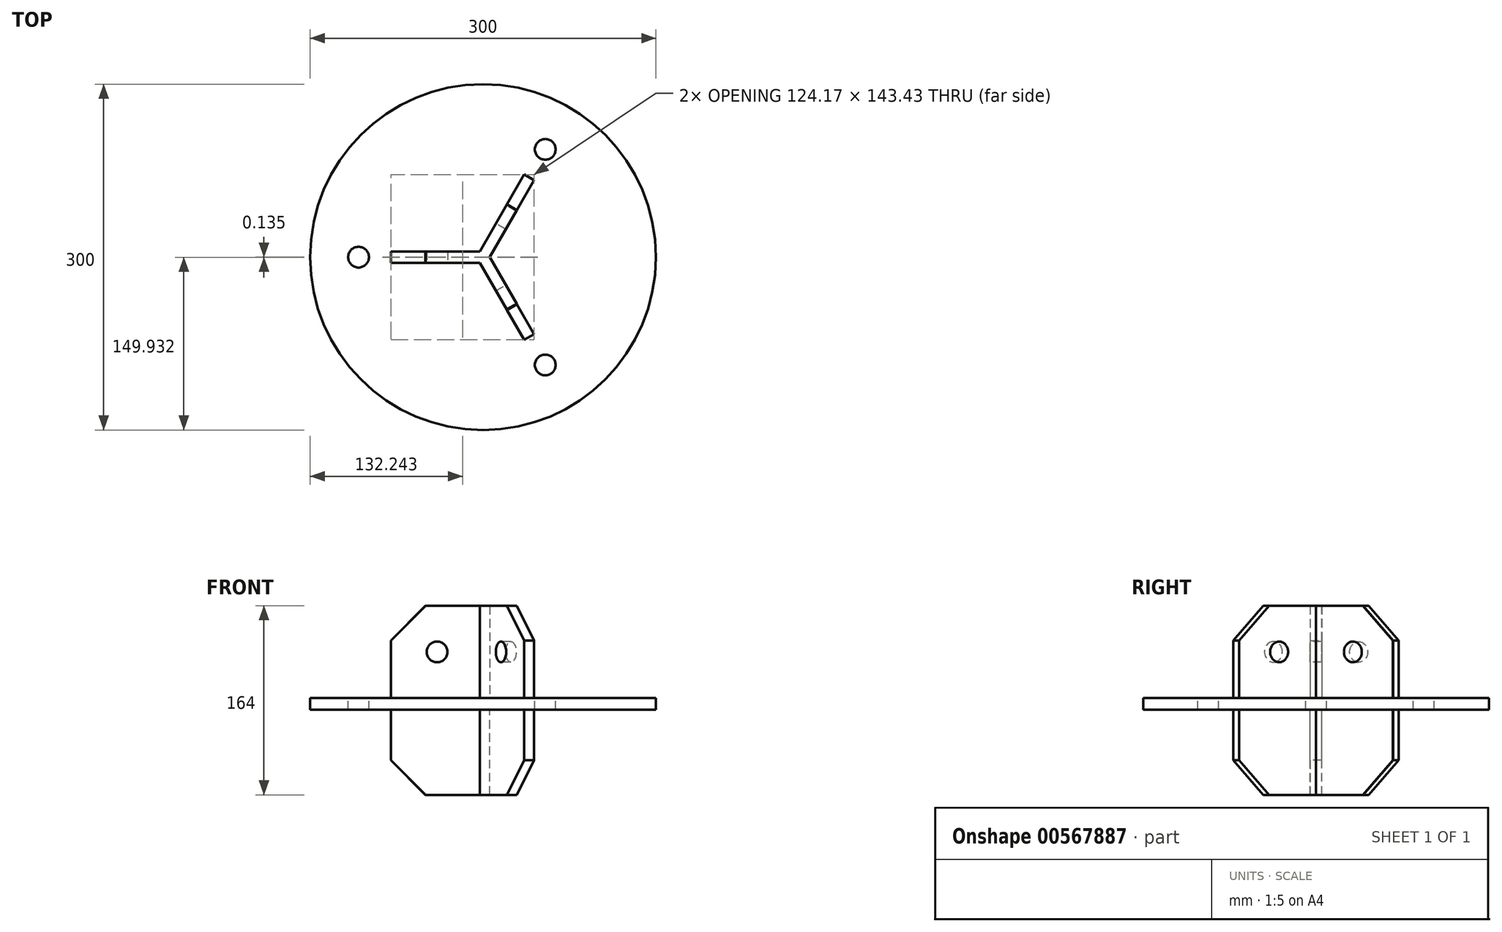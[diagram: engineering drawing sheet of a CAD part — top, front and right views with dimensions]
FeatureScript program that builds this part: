
annotation { "Feature Type Name" : "Feature", "Feature Type Description" : "" }
export const myFeature = defineFeature(function(context is Context, id is Id, definition is map)
    precondition{}
    {
        {
            var Q0;
            Q0=qCreatedBy(makeId("Top.planeOp"),FACE);
            var sketch = newSketch(context, id + "F0", { "sketchPlane" : qUnion([Q0])});
            skCircle(sketch, "E0", {"center": v(0, 0) * mm, "radius": 150 * mm});
            skSolve(sketch);
        }
        {
            var Q0;
            Q0=makeQuery(id+"F0.imprint","IMPRINT",FACE,{"disambiguationData":[TD([[makeQuery(id+"F0.imprint","IMPRINT",EDGE,{"derivedFrom":sQuery(id+"F0.wireOp",EDGE,"E0")}),1.0]])]});
            extrude(context, id + "F1", {"entities" : qUnion([Q0]), "depth" : 10 * mm, "offsetDistance" : 25 * mm});
        }
        {
            var Q0;
            Q0=makeQuery(id+"F1.opExtrude","CAP_FACE",FACE,{"disambiguationData":[OSD([sQuery(id+"F0.wireOp",EDGE,"E0"),sQuery(id+"F0.wireOp",EDGE,"oJbW3ULZ-2pRP-CatU-Atqn-FDPEkCRfx0l3")])],"isStart":false});
            var sketch = newSketch(context, id + "F2", { "sketchPlane" : qUnion([Q0])});
            skCircle(sketch, "E1", {"center": v(-108, 0) * mm, "radius": 9 * mm});
            skCircle(sketch, "E2", {"center": v(54, -93.53) * mm, "radius": 9 * mm});
            skCircle(sketch, "E3", {"center": v(54, 93.53) * mm, "radius": 9 * mm});
            skCircle(sketch, "E4", {"center": v(0, 0) * mm, "radius": 108 * mm, "construction": true});
            skLineSegment(sketch, "E5", {"start": v(54, 93.53) * mm, "end": v(0, 0) * mm});
            skLineSegment(sketch, "E6", {"start": v(0, 0) * mm, "end": v(-108, 0) * mm});
            skLineSegment(sketch, "E7", {"start": v(0, 0) * mm, "end": v(54, -93.53) * mm});
            skSolve(sketch);
        }
        {
            var Q0;
            Q0=qSketchRegion(id+"F2",true);
            extrude(context, id + "F3", {"entities" : qUnion([Q0]), "operationType" : NewBodyOperationType.REMOVE, "oppositeDirection" : true, "depth" : 25 * mm, "offsetDistance" : 25 * mm});
        }
        {
            var Q0;
            Q0=makeQuery(id+"F1.opExtrude","CAP_FACE",FACE,{"disambiguationData":[OSD([sQuery(id+"F0.wireOp",EDGE,"E0")])],"isStart":false});
            var sketch = newSketch(context, id + "F4", { "sketchPlane" : qUnion([Q0])});
            skLineSegment(sketch, "E8", {"start": v(0, 0) * mm, "end": v(54, -93.53) * mm, "construction": true});
            skLineSegment(sketch, "E9", {"start": v(0, 0) * mm, "end": v(-108, 0) * mm, "construction": true});
            skLineSegment(sketch, "E10", {"start": v(0, 0) * mm, "end": v(54, 93.53) * mm, "construction": true});
            skLineSegment(sketch, "E11.0", {"start": v(-2.89, 5) * mm, "end": v(-79.84, 5) * mm});
            skLineSegment(sketch, "E11.1", {"start": v(-2.89, 5) * mm, "end": v(35.6, 71.65) * mm});
            skLineSegment(sketch, "E12.0", {"start": v(-2.89, -5) * mm, "end": v(-79.84, -5) * mm});
            skLineSegment(sketch, "E12.1", {"start": v(-2.89, -5) * mm, "end": v(35.67, -71.78) * mm});
            skLineSegment(sketch, "E13.0", {"start": v(5.77, 0) * mm, "end": v(44.33, -66.78) * mm});
            skLineSegment(sketch, "E13.1", {"start": v(5.77, 0) * mm, "end": v(44.25, 66.65) * mm});
            skLineSegment(sketch, "E14", {"start": v(44.33, -66.78) * mm, "end": v(35.67, -71.78) * mm});
            skLineSegment(sketch, "E15", {"start": v(44.25, 66.65) * mm, "end": v(35.6, 71.65) * mm});
            skLineSegment(sketch, "E16", {"start": v(-79.84, 5) * mm, "end": v(-79.84, -5) * mm});
            skCircle(sketch, "E17", {"center": v(0, 0) * mm, "radius": 80 * mm, "construction": true});
            skSolve(sketch);
        }
        {
            var Q0;
            Q0=makeQuery(id+"F4.imprint","IMPRINT",FACE,{"disambiguationData":[TD([[makeQuery(id+"F4.imprint","IMPRINT",EDGE,{"derivedFrom":sQuery(id+"F4.wireOp",EDGE,"E11.0")}),1.0]])]});
            extrude(context, id + "F5", {"entities" : qUnion([Q0]), "depth" : 80 * mm, "offsetDistance" : 25 * mm});
        }
        {
            var Q0;
            Q0=qCreatedBy(makeId("Top.planeOp"),FACE);
            cPlane(context, id + "F6", {"entities" : qUnion([Q0]), "cplaneType" : CPlaneType.OFFSET, "offset" : 8 * mm, "width" : 150 * mm, "height" : 150 * mm});
        }
        {
            var Q0;
            Q0=makeQuery(id+"F5.opExtrude","SWEPT_BODY",BODY,{"disambiguationData":[OSD([sQuery(id+"F4.wireOp",EDGE,"E11.0"),sQuery(id+"F4.wireOp",EDGE,"E11.1"),sQuery(id+"F4.wireOp",EDGE,"E12.0"),sQuery(id+"F4.wireOp",EDGE,"E12.1"),sQuery(id+"F4.wireOp",EDGE,"E13.0"),sQuery(id+"F4.wireOp",EDGE,"E13.1"),sQuery(id+"F4.wireOp",EDGE,"E14"),sQuery(id+"F4.wireOp",EDGE,"E15"),sQuery(id+"F4.wireOp",EDGE,"E16")])]});
            var Q1;
            Q1=qCreatedBy(id+"F6.planeOp",FACE);
            mirror(context, id + "F7", {"operationType" : NewBodyOperationType.ADD, "entities" : qUnion([Q0]), "mirrorPlane" : qUnion([Q1])});
        }
        {
            var Q0;
            Q0=makeQuery(id+"F5.opExtrude","CAP_EDGE",EDGE,{"disambiguationData":[OSD([sQuery(id+"F4.wireOp",EDGE,"E16")])],"isStart":false});
            var Q1;
            Q1=makeQuery(id+"F5.opExtrude","CAP_EDGE",EDGE,{"disambiguationData":[OSD([sQuery(id+"F4.wireOp",EDGE,"E15")])],"isStart":false});
            var Q2;
            Q2=makeQuery(id+"F5.opExtrude","CAP_EDGE",EDGE,{"disambiguationData":[OSD([sQuery(id+"F4.wireOp",EDGE,"E14")])],"isStart":false});
            var Q3;
            Q3=makeQuery(id+"F7.opPattern","COPY",EDGE,{"derivedFrom":makeQuery(id+"F5.opExtrude","CAP_EDGE",EDGE,{"disambiguationData":[OSD([sQuery(id+"F4.wireOp",EDGE,"E15")])],"isStart":false}),"instanceName":"1"});
            var Q4;
            Q4=makeQuery(id+"F7.opPattern","COPY",EDGE,{"derivedFrom":makeQuery(id+"F5.opExtrude","CAP_EDGE",EDGE,{"disambiguationData":[OSD([sQuery(id+"F4.wireOp",EDGE,"E16")])],"isStart":false}),"instanceName":"1"});
            var Q5;
            Q5=makeQuery(id+"F7.opPattern","COPY",EDGE,{"derivedFrom":makeQuery(id+"F5.opExtrude","CAP_EDGE",EDGE,{"disambiguationData":[OSD([sQuery(id+"F4.wireOp",EDGE,"E14")])],"isStart":false}),"instanceName":"1"});
            chamfer(context, id + "F8", {"entities" : qUnion([Q0, Q1, Q2, Q3, Q4, Q5]), "width" : 30 * mm, "tangentPropagation" : true});
        }
        {
            var Q0;
            Q0=makeQuery(id+"F5.opExtrude","SWEPT_FACE",FACE,{"disambiguationData":[OSD([sQuery(id+"F4.wireOp",EDGE,"E11.1")])]});
            var sketch = newSketch(context, id + "F9", { "sketchPlane" : qUnion([Q0])});
            skCircle(sketch, "E18", {"center": v(-39.84, 50) * mm, "radius": 9 * mm});
            skSolve(sketch);
        }
        {
            var Q0;
            Q0=qSketchRegion(id+"F9",true);
            extrude(context, id + "F10", {"entities" : qUnion([Q0]), "operationType" : NewBodyOperationType.REMOVE, "oppositeDirection" : true, "depth" : 25 * mm, "offsetDistance" : 25 * mm});
        }
        {
            var Q0;
            Q0=makeQuery(id+"F1.opExtrude","SWEPT_BODY",BODY,{"disambiguationData":[OSD([sQuery(id+"F0.wireOp",EDGE,"E0")])]});
            var Q1;
            Q1=makeQuery(id+"F1.opExtrude","SWEPT_FACE",FACE,{"disambiguationData":[OSD([sQuery(id+"F0.wireOp",EDGE,"E0")])]});
            circularPattern(context, id + "F11", {"entities" : qUnion([Q0]), "axis" : qUnion([Q1]), "angle" : 360 * degree, "instanceCount" : 3, "equalSpace" : true});
        }
    });
